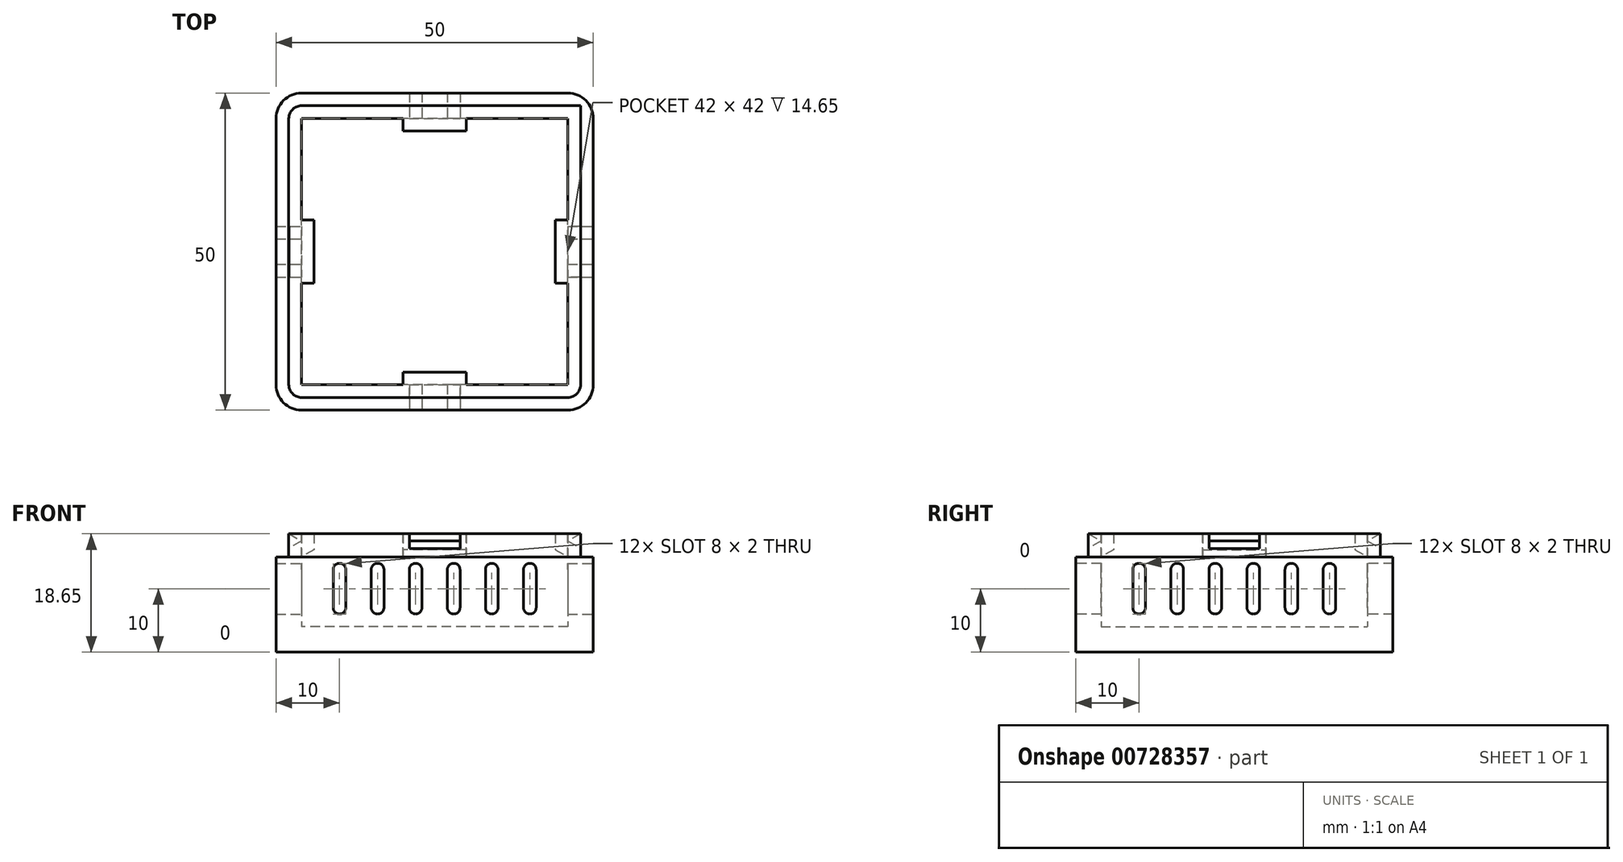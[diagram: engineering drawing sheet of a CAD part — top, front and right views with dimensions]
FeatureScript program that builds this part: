
annotation { "Feature Type Name" : "Feature", "Feature Type Description" : "" }
export const myFeature = defineFeature(function(context is Context, id is Id, definition is map)
    precondition{}
    {
        {
            var Q0;
            Q0=qCreatedBy(makeId("Top.planeOp"),FACE);
            var sketch = newSketch(context, id + "F0", { "sketchPlane" : qUnion([Q0])});
            skLineSegment(sketch, "E0.bottom", {"start": v(25, -25) * mm, "end": v(-25, -25) * mm});
            skLineSegment(sketch, "E0.top", {"start": v(25, 25) * mm, "end": v(-25, 25) * mm});
            skLineSegment(sketch, "E0.left", {"start": v(25, -25) * mm, "end": v(25, 25) * mm});
            skLineSegment(sketch, "E0.right", {"start": v(-25, -25) * mm, "end": v(-25, 25) * mm});
            skPoint(sketch, "E0.middle", {"position": v(0, 0) * mm});
            skSolve(sketch);
        }
        {
            var Q0;
            Q0=qSketchRegion(id+"F0",true);
            extrude(context, id + "F1", {"entities" : qUnion([Q0]), "depth" : 20 * mm, "offsetDistance" : 25 * mm});
        }
        {
            var Q0;
            Q0=makeQuery(id+"F1.opExtrude","CAP_FACE",FACE,{"disambiguationData":[OSD([sQuery(id+"F0.wireOp",EDGE,"E0.bottom"),sQuery(id+"F0.wireOp",EDGE,"E0.top"),sQuery(id+"F0.wireOp",EDGE,"E0.left"),sQuery(id+"F0.wireOp",EDGE,"E0.right")])],"isStart":false});
            shell(context, id + "F2", {"entities" : qUnion([Q0]), "thickness" : 4 * mm});
        }
        {
            var Q0;
            Q0=makeQuery(id+"F1.opExtrude","SWEPT_EDGE",EDGE,{"disambiguationData":[OSD([sQuery(id+"F0.wireOp",EDGE,"E0.bottom"),sQuery(id+"F0.wireOp",EDGE,"E0.right")])]});
            var Q1;
            Q1=makeQuery(id+"F1.opExtrude","SWEPT_EDGE",EDGE,{"disambiguationData":[OSD([sQuery(id+"F0.wireOp",EDGE,"E0.bottom"),sQuery(id+"F0.wireOp",EDGE,"E0.left")])]});
            var Q2;
            Q2=makeQuery(id+"F1.opExtrude","SWEPT_EDGE",EDGE,{"disambiguationData":[OSD([sQuery(id+"F0.wireOp",EDGE,"E0.top"),sQuery(id+"F0.wireOp",EDGE,"E0.left")])]});
            var Q3;
            Q3=makeQuery(id+"F1.opExtrude","SWEPT_EDGE",EDGE,{"disambiguationData":[OSD([sQuery(id+"F0.wireOp",EDGE,"E0.top"),sQuery(id+"F0.wireOp",EDGE,"E0.right")])]});
            fillet(context, id + "F3", {"entities" : qUnion([Q0, Q1, Q2, Q3]), "radius" : 4 * mm, "tangentPropagation" : true, "allowEdgeOverflow" : false});
        }
        {
            var Q0;
            Q0=makeQuery(id+"F1.opExtrude","SWEPT_FACE",FACE,{"disambiguationData":[OSD([sQuery(id+"F0.wireOp",EDGE,"E0.bottom")])]});
            var sketch = newSketch(context, id + "F4", { "sketchPlane" : qUnion([Q0])});
            skLineSegment(sketch, "E1.bottom", {"start": v(-15, 6) * mm, "end": v(-15, 6) * mm});
            skLineSegment(sketch, "E1.top", {"start": v(-15, 14) * mm, "end": v(-15, 14) * mm});
            skLineSegment(sketch, "E1.left", {"start": v(-14, 7) * mm, "end": v(-14, 13) * mm});
            skLineSegment(sketch, "E1.right", {"start": v(-16, 7) * mm, "end": v(-16, 13) * mm});
            skPoint(sketch, "E1.middle", {"position": v(-15, 10) * mm});
            skLineSegment(sketch, "E2.1.0.0", {"start": v(-9, 14) * mm, "end": v(-9, 14) * mm});
            skLineSegment(sketch, "E2.1.0.1", {"start": v(-10, 7) * mm, "end": v(-10, 13) * mm});
            skLineSegment(sketch, "E2.1.0.2", {"start": v(-9, 6) * mm, "end": v(-9, 6) * mm});
            skLineSegment(sketch, "E2.1.0.3", {"start": v(-8, 7) * mm, "end": v(-8, 13) * mm});
            skPoint(sketch, "E2.1.0.4", {"position": v(-9, 10) * mm});
            skLineSegment(sketch, "E2.2.0.0", {"start": v(-3, 14) * mm, "end": v(-3, 14) * mm});
            skLineSegment(sketch, "E2.2.0.1", {"start": v(-4, 7) * mm, "end": v(-4, 13) * mm});
            skLineSegment(sketch, "E2.2.0.2", {"start": v(-3, 6) * mm, "end": v(-3, 6) * mm});
            skLineSegment(sketch, "E2.2.0.3", {"start": v(-2, 7) * mm, "end": v(-2, 13) * mm});
            skPoint(sketch, "E2.2.0.4", {"position": v(-3, 10) * mm});
            skLineSegment(sketch, "E2.3.0.0", {"start": v(3, 14) * mm, "end": v(3, 14) * mm});
            skLineSegment(sketch, "E2.3.0.1", {"start": v(2, 7) * mm, "end": v(2, 13) * mm});
            skLineSegment(sketch, "E2.3.0.2", {"start": v(3, 6) * mm, "end": v(3, 6) * mm});
            skLineSegment(sketch, "E2.3.0.3", {"start": v(4, 7) * mm, "end": v(4, 13) * mm});
            skPoint(sketch, "E2.3.0.4", {"position": v(3, 10) * mm});
            skLineSegment(sketch, "E2.4.0.0", {"start": v(9, 14) * mm, "end": v(9, 14) * mm});
            skLineSegment(sketch, "E2.4.0.1", {"start": v(8, 7) * mm, "end": v(8, 13) * mm});
            skLineSegment(sketch, "E2.4.0.2", {"start": v(9, 6) * mm, "end": v(9, 6) * mm});
            skLineSegment(sketch, "E2.4.0.3", {"start": v(10, 7) * mm, "end": v(10, 13) * mm});
            skPoint(sketch, "E2.4.0.4", {"position": v(9, 10) * mm});
            skLineSegment(sketch, "E2.direction1", {"start": v(-16, 6) * mm, "end": v(-10, 6) * mm, "construction": true});
            skLineSegment(sketch, "E3.MirrorCS", {"start": v(15, 6) * mm, "end": v(15, 6) * mm});
            skLineSegment(sketch, "E4.MirrorCS", {"start": v(16, 7) * mm, "end": v(16, 13) * mm});
            skLineSegment(sketch, "E5.MirrorCS", {"start": v(14, 7) * mm, "end": v(14, 13) * mm});
            skLineSegment(sketch, "E6.MirrorCS", {"start": v(15, 14) * mm, "end": v(15, 14) * mm});
            skPoint(sketch, "E7.MirrorP", {"position": v(15, 10) * mm});
            skLineSegment(sketch, "E8.MirrorCS", {"start": v(16, 6) * mm, "end": v(10, 6) * mm, "construction": true});
            skPoint(sketch, "E9.visualSharp", {"position": v(-16, 14) * mm});
            skArc(sketch, "E9.filletArc", {"start": v(-15, 14) * mm, "mid": v(-15.7, 13.7) * mm, "end": v(-16, 13) * mm});
            skPoint(sketch, "E10.visualSharp", {"position": v(-14, 14) * mm});
            skArc(sketch, "E10.filletArc", {"start": v(-14, 13) * mm, "mid": v(-14.3, 13.7) * mm, "end": v(-15, 14) * mm});
            skPoint(sketch, "E11.visualSharp", {"position": v(-16, 6) * mm});
            skArc(sketch, "E11.filletArc", {"start": v(-16, 7) * mm, "mid": v(-15.7, 6.3) * mm, "end": v(-15, 6) * mm});
            skPoint(sketch, "E12.visualSharp", {"position": v(-14, 6) * mm});
            skArc(sketch, "E12.filletArc", {"start": v(-15, 6) * mm, "mid": v(-14.3, 6.3) * mm, "end": v(-14, 7) * mm});
            skPoint(sketch, "E13.visualSharp", {"position": v(-10, 14) * mm});
            skArc(sketch, "E13.filletArc", {"start": v(-9, 14) * mm, "mid": v(-9.7, 13.7) * mm, "end": v(-10, 13) * mm});
            skPoint(sketch, "E14.visualSharp", {"position": v(-8, 14) * mm});
            skArc(sketch, "E14.filletArc", {"start": v(-8, 13) * mm, "mid": v(-8.3, 13.7) * mm, "end": v(-9, 14) * mm});
            skPoint(sketch, "E15.visualSharp", {"position": v(-8, 6) * mm});
            skArc(sketch, "E15.filletArc", {"start": v(-9, 6) * mm, "mid": v(-8.3, 6.3) * mm, "end": v(-8, 7) * mm});
            skPoint(sketch, "E16.visualSharp", {"position": v(-10, 6) * mm});
            skArc(sketch, "E16.filletArc", {"start": v(-10, 7) * mm, "mid": v(-9.7, 6.3) * mm, "end": v(-9, 6) * mm});
            skPoint(sketch, "E17.visualSharp", {"position": v(-4, 6) * mm});
            skArc(sketch, "E17.filletArc", {"start": v(-4, 7) * mm, "mid": v(-3.7, 6.3) * mm, "end": v(-3, 6) * mm});
            skPoint(sketch, "E18.visualSharp", {"position": v(-2, 6) * mm});
            skArc(sketch, "E18.filletArc", {"start": v(-3, 6) * mm, "mid": v(-2.3, 6.3) * mm, "end": v(-2, 7) * mm});
            skPoint(sketch, "E19.visualSharp", {"position": v(-2, 14) * mm});
            skArc(sketch, "E19.filletArc", {"start": v(-2, 13) * mm, "mid": v(-2.3, 13.7) * mm, "end": v(-3, 14) * mm});
            skPoint(sketch, "E20.visualSharp", {"position": v(-4, 14) * mm});
            skArc(sketch, "E20.filletArc", {"start": v(-3, 14) * mm, "mid": v(-3.7, 13.7) * mm, "end": v(-4, 13) * mm});
            skPoint(sketch, "E21.visualSharp", {"position": v(2, 14) * mm});
            skArc(sketch, "E21.filletArc", {"start": v(3, 14) * mm, "mid": v(2.3, 13.7) * mm, "end": v(2, 13) * mm});
            skPoint(sketch, "E22.visualSharp", {"position": v(4, 14) * mm});
            skArc(sketch, "E22.filletArc", {"start": v(4, 13) * mm, "mid": v(3.7, 13.7) * mm, "end": v(3, 14) * mm});
            skPoint(sketch, "E23.visualSharp", {"position": v(4, 6) * mm});
            skArc(sketch, "E23.filletArc", {"start": v(3, 6) * mm, "mid": v(3.7, 6.3) * mm, "end": v(4, 7) * mm});
            skPoint(sketch, "E24.visualSharp", {"position": v(2, 6) * mm});
            skArc(sketch, "E24.filletArc", {"start": v(2, 7) * mm, "mid": v(2.3, 6.3) * mm, "end": v(3, 6) * mm});
            skPoint(sketch, "E25.visualSharp", {"position": v(10, 14) * mm});
            skArc(sketch, "E25.filletArc", {"start": v(10, 13) * mm, "mid": v(9.7, 13.7) * mm, "end": v(9, 14) * mm});
            skPoint(sketch, "E26.visualSharp", {"position": v(8, 14) * mm});
            skArc(sketch, "E26.filletArc", {"start": v(9, 14) * mm, "mid": v(8.3, 13.7) * mm, "end": v(8, 13) * mm});
            skPoint(sketch, "E27.visualSharp", {"position": v(8, 6) * mm});
            skArc(sketch, "E27.filletArc", {"start": v(8, 7) * mm, "mid": v(8.3, 6.3) * mm, "end": v(9, 6) * mm});
            skPoint(sketch, "E28.visualSharp", {"position": v(10, 6) * mm});
            skArc(sketch, "E28.filletArc", {"start": v(9, 6) * mm, "mid": v(9.7, 6.3) * mm, "end": v(10, 7) * mm});
            skPoint(sketch, "E29.visualSharp", {"position": v(16, 14) * mm});
            skArc(sketch, "E29.filletArc", {"start": v(16, 13) * mm, "mid": v(15.7, 13.7) * mm, "end": v(15, 14) * mm});
            skPoint(sketch, "E30.visualSharp", {"position": v(14, 14) * mm});
            skArc(sketch, "E30.filletArc", {"start": v(15, 14) * mm, "mid": v(14.3, 13.7) * mm, "end": v(14, 13) * mm});
            skPoint(sketch, "E31.visualSharp", {"position": v(16, 6) * mm});
            skArc(sketch, "E31.filletArc", {"start": v(15, 6) * mm, "mid": v(15.7, 6.3) * mm, "end": v(16, 7) * mm});
            skPoint(sketch, "E32.visualSharp", {"position": v(14, 6) * mm});
            skArc(sketch, "E32.filletArc", {"start": v(14, 7) * mm, "mid": v(14.3, 6.3) * mm, "end": v(15, 6) * mm});
            skSolve(sketch);
        }
        {
            var Q0;
            Q0=qSketchRegion(id+"F4",true);
            extrude(context, id + "F5", {"entities" : qUnion([Q0]), "operationType" : NewBodyOperationType.REMOVE, "oppositeDirection" : true, "depth" : 50 * mm, "offsetDistance" : 25 * mm});
        }
        {
            var Q0;
            Q0=makeQuery(id+"F1.opExtrude","SWEPT_FACE",FACE,{"disambiguationData":[OSD([sQuery(id+"F0.wireOp",EDGE,"E0.left")])]});
            var sketch = newSketch(context, id + "F6", { "sketchPlane" : qUnion([Q0])});
            skLineSegment(sketch, "E33.bottom", {"start": v(-15, 6) * mm, "end": v(-15, 6) * mm});
            skLineSegment(sketch, "E33.top", {"start": v(-15, 14) * mm, "end": v(-15, 14) * mm});
            skLineSegment(sketch, "E33.left", {"start": v(-14, 7) * mm, "end": v(-14, 13) * mm});
            skLineSegment(sketch, "E33.right", {"start": v(-16, 7) * mm, "end": v(-16, 13) * mm});
            skPoint(sketch, "E33.middle", {"position": v(-15, 10) * mm});
            skPoint(sketch, "E34.visualSharp", {"position": v(-16, 14) * mm});
            skArc(sketch, "E34.filletArc", {"start": v(-15, 14) * mm, "mid": v(-15.7, 13.7) * mm, "end": v(-16, 13) * mm});
            skPoint(sketch, "E35.visualSharp", {"position": v(-14, 14) * mm});
            skArc(sketch, "E35.filletArc", {"start": v(-14, 13) * mm, "mid": v(-14.3, 13.7) * mm, "end": v(-15, 14) * mm});
            skPoint(sketch, "E36.visualSharp", {"position": v(-14, 6) * mm});
            skArc(sketch, "E36.filletArc", {"start": v(-15, 6) * mm, "mid": v(-14.3, 6.3) * mm, "end": v(-14, 7) * mm});
            skPoint(sketch, "E37.visualSharp", {"position": v(-16, 6) * mm});
            skArc(sketch, "E37.filletArc", {"start": v(-16, 7) * mm, "mid": v(-15.7, 6.3) * mm, "end": v(-15, 6) * mm});
            skPoint(sketch, "E38.1.0.0", {"position": v(-8, 6) * mm});
            skPoint(sketch, "E38.1.0.1", {"position": v(-10, 6) * mm});
            skLineSegment(sketch, "E38.1.0.2", {"start": v(-10, 7) * mm, "end": v(-10, 13) * mm});
            skLineSegment(sketch, "E38.1.0.3", {"start": v(-8, 7) * mm, "end": v(-8, 13) * mm});
            skPoint(sketch, "E38.1.0.4", {"position": v(-8, 14) * mm});
            skPoint(sketch, "E38.1.0.5", {"position": v(-10, 14) * mm});
            skPoint(sketch, "E38.1.0.6", {"position": v(-9, 10) * mm});
            skArc(sketch, "E38.1.0.7", {"start": v(-9, 6) * mm, "mid": v(-8.3, 6.3) * mm, "end": v(-8, 7) * mm});
            skArc(sketch, "E38.1.0.8", {"start": v(-8, 13) * mm, "mid": v(-8.3, 13.7) * mm, "end": v(-9, 14) * mm});
            skArc(sketch, "E38.1.0.9", {"start": v(-9, 14) * mm, "mid": v(-9.7, 13.7) * mm, "end": v(-10, 13) * mm});
            skArc(sketch, "E38.1.0.10", {"start": v(-10, 7) * mm, "mid": v(-9.7, 6.3) * mm, "end": v(-9, 6) * mm});
            skPoint(sketch, "E38.2.0.0", {"position": v(-2, 6) * mm});
            skPoint(sketch, "E38.2.0.1", {"position": v(-4, 6) * mm});
            skLineSegment(sketch, "E38.2.0.2", {"start": v(-4, 7) * mm, "end": v(-4, 13) * mm});
            skLineSegment(sketch, "E38.2.0.3", {"start": v(-2, 7) * mm, "end": v(-2, 13) * mm});
            skPoint(sketch, "E38.2.0.4", {"position": v(-2, 14) * mm});
            skPoint(sketch, "E38.2.0.5", {"position": v(-4, 14) * mm});
            skPoint(sketch, "E38.2.0.6", {"position": v(-3, 10) * mm});
            skArc(sketch, "E38.2.0.7", {"start": v(-3, 6) * mm, "mid": v(-2.3, 6.3) * mm, "end": v(-2, 7) * mm});
            skArc(sketch, "E38.2.0.8", {"start": v(-2, 13) * mm, "mid": v(-2.3, 13.7) * mm, "end": v(-3, 14) * mm});
            skArc(sketch, "E38.2.0.9", {"start": v(-3, 14) * mm, "mid": v(-3.7, 13.7) * mm, "end": v(-4, 13) * mm});
            skArc(sketch, "E38.2.0.10", {"start": v(-4, 7) * mm, "mid": v(-3.7, 6.3) * mm, "end": v(-3, 6) * mm});
            skLineSegment(sketch, "E38.direction1", {"start": v(-16, 6) * mm, "end": v(-10, 6) * mm, "construction": true});
            skArc(sketch, "E39.MirrorCS", {"start": v(10, 7) * mm, "mid": v(9.7, 6.3) * mm, "end": v(9, 6) * mm});
            skArc(sketch, "E40.MirrorCS", {"start": v(9, 14) * mm, "mid": v(9.7, 13.7) * mm, "end": v(10, 13) * mm});
            skArc(sketch, "E41.MirrorCS", {"start": v(9, 6) * mm, "mid": v(8.3, 6.3) * mm, "end": v(8, 7) * mm});
            skArc(sketch, "E42.MirrorCS", {"start": v(16, 7) * mm, "mid": v(15.7, 6.3) * mm, "end": v(15, 6) * mm});
            skArc(sketch, "E43.MirrorCS", {"start": v(15, 6) * mm, "mid": v(14.3, 6.3) * mm, "end": v(14, 7) * mm});
            skArc(sketch, "E44.MirrorCS", {"start": v(14, 13) * mm, "mid": v(14.3, 13.7) * mm, "end": v(15, 14) * mm});
            skArc(sketch, "E45.MirrorCS", {"start": v(2, 13) * mm, "mid": v(2.3, 13.7) * mm, "end": v(3, 14) * mm});
            skArc(sketch, "E46.MirrorCS", {"start": v(3, 6) * mm, "mid": v(2.3, 6.3) * mm, "end": v(2, 7) * mm});
            skArc(sketch, "E47.MirrorCS", {"start": v(4, 7) * mm, "mid": v(3.7, 6.3) * mm, "end": v(3, 6) * mm});
            skArc(sketch, "E48.MirrorCS", {"start": v(8, 13) * mm, "mid": v(8.3, 13.7) * mm, "end": v(9, 14) * mm});
            skArc(sketch, "E49.MirrorCS", {"start": v(15, 14) * mm, "mid": v(15.7, 13.7) * mm, "end": v(16, 13) * mm});
            skArc(sketch, "E50.MirrorCS", {"start": v(3, 14) * mm, "mid": v(3.7, 13.7) * mm, "end": v(4, 13) * mm});
            skPoint(sketch, "E51.MirrorP", {"position": v(9, 10) * mm});
            skLineSegment(sketch, "E52.MirrorCS", {"start": v(4, 7) * mm, "end": v(4, 13) * mm});
            skLineSegment(sketch, "E53.MirrorCS", {"start": v(16, 6) * mm, "end": v(10, 6) * mm, "construction": true});
            skPoint(sketch, "E54.MirrorP", {"position": v(14, 14) * mm});
            skLineSegment(sketch, "E55.MirrorCS", {"start": v(8, 7) * mm, "end": v(8, 13) * mm});
            skPoint(sketch, "E56.MirrorP", {"position": v(4, 6) * mm});
            skPoint(sketch, "E57.MirrorP", {"position": v(14, 6) * mm});
            skPoint(sketch, "E58.MirrorP", {"position": v(4, 14) * mm});
            skLineSegment(sketch, "E59.MirrorCS", {"start": v(10, 7) * mm, "end": v(10, 13) * mm});
            skPoint(sketch, "E60.MirrorP", {"position": v(10, 6) * mm});
            skLineSegment(sketch, "E61.MirrorCS", {"start": v(15, 14) * mm, "end": v(15, 14) * mm});
            skLineSegment(sketch, "E62.MirrorCS", {"start": v(16, 7) * mm, "end": v(16, 13) * mm});
            skLineSegment(sketch, "E63.MirrorCS", {"start": v(14, 7) * mm, "end": v(14, 13) * mm});
            skLineSegment(sketch, "E64.MirrorCS", {"start": v(2, 7) * mm, "end": v(2, 13) * mm});
            skPoint(sketch, "E65.MirrorP", {"position": v(16, 14) * mm});
            skPoint(sketch, "E66.MirrorP", {"position": v(8, 14) * mm});
            skPoint(sketch, "E67.MirrorP", {"position": v(16, 6) * mm});
            skPoint(sketch, "E68.MirrorP", {"position": v(2, 14) * mm});
            skPoint(sketch, "E69.MirrorP", {"position": v(2, 6) * mm});
            skPoint(sketch, "E70.MirrorP", {"position": v(3, 10) * mm});
            skLineSegment(sketch, "E71.MirrorCS", {"start": v(15, 6) * mm, "end": v(15, 6) * mm});
            skPoint(sketch, "E72.MirrorP", {"position": v(15, 10) * mm});
            skPoint(sketch, "E73.MirrorP", {"position": v(8, 6) * mm});
            skPoint(sketch, "E74.MirrorP", {"position": v(10, 14) * mm});
            skSolve(sketch);
        }
        {
            var Q0;
            Q0=qSketchRegion(id+"F6",true);
            extrude(context, id + "F7", {"entities" : qUnion([Q0]), "operationType" : NewBodyOperationType.REMOVE, "endBound" : BoundingType.THROUGH_ALL, "oppositeDirection" : true, "depth" : 25 * mm, "offsetDistance" : 25 * mm});
        }
        {
            var Q0;
            Q0=makeQuery(id+"F1.opExtrude","CAP_FACE",FACE,{"disambiguationData":[OSD([sQuery(id+"F0.wireOp",EDGE,"E0.bottom"),sQuery(id+"F0.wireOp",EDGE,"E0.top"),sQuery(id+"F0.wireOp",EDGE,"E0.left"),sQuery(id+"F0.wireOp",EDGE,"E0.right")])],"isStart":false});
            var sketch = newSketch(context, id + "F8", { "sketchPlane" : qUnion([Q0])});
            skLineSegment(sketch, "E75.bottom", {"start": v(25, 25) * mm, "end": v(-25, 25) * mm});
            skLineSegment(sketch, "E75.top", {"start": v(25, -25) * mm, "end": v(-25, -25) * mm});
            skLineSegment(sketch, "E75.left", {"start": v(25, 25) * mm, "end": v(25, -25) * mm});
            skLineSegment(sketch, "E75.right", {"start": v(-25, 25) * mm, "end": v(-25, -25) * mm});
            skPoint(sketch, "E75.middle", {"position": v(0, 0) * mm});
            skLineSegment(sketch, "E76.bottom", {"start": v(23, 23) * mm, "end": v(-23, 23) * mm});
            skLineSegment(sketch, "E76.top", {"start": v(23, -23) * mm, "end": v(-23, -23) * mm});
            skLineSegment(sketch, "E76.left", {"start": v(23, 23) * mm, "end": v(23, -23) * mm});
            skLineSegment(sketch, "E76.right", {"start": v(-23, 23) * mm, "end": v(-23, -23) * mm});
            skSolve(sketch);
        }
        {
            var Q0;
            Q0=qSketchRegion(id+"F8",true);
            extrude(context, id + "F9", {"entities" : qUnion([Q0]), "operationType" : NewBodyOperationType.REMOVE, "oppositeDirection" : true, "depth" : 5 * mm, "offsetDistance" : 25 * mm});
        }
        {
            var Q0;
            Q0=makeQuery(id+"F9.boolean.opBoolean","COPY",EDGE,{"derivedFrom":makeQuery(id+"F9.opExtrude","SWEPT_EDGE",EDGE,{"disambiguationData":[OSD([sQuery(id+"F8.wireOp",EDGE,"E76.bottom"),sQuery(id+"F8.wireOp",EDGE,"E76.right")])]})});
            var Q1;
            Q1=makeQuery(id+"F9.boolean.opBoolean","COPY",EDGE,{"derivedFrom":makeQuery(id+"F9.opExtrude","SWEPT_EDGE",EDGE,{"disambiguationData":[OSD([sQuery(id+"F8.wireOp",EDGE,"E76.top"),sQuery(id+"F8.wireOp",EDGE,"E76.right")])]})});
            var Q2;
            Q2=makeQuery(id+"F9.boolean.opBoolean","COPY",EDGE,{"derivedFrom":makeQuery(id+"F9.opExtrude","SWEPT_EDGE",EDGE,{"disambiguationData":[OSD([sQuery(id+"F8.wireOp",EDGE,"E76.top"),sQuery(id+"F8.wireOp",EDGE,"E76.left")])]})});
            fillet(context, id + "F10", {"entities" : qUnion([Q0, Q1, Q2]), "radius" : 2 * mm, "tangentPropagation" : true, "allowEdgeOverflow" : false});
        }
        {
            var Q0;
            Q0=qCreatedBy(makeId("Right.planeOp"),FACE);
            var sketch = newSketch(context, id + "F11", { "sketchPlane" : qUnion([Q0])});
            skLineSegment(sketch, "E77", {"start": v(21, 20) * mm, "end": v(19, 18.85) * mm});
            skLineSegment(sketch, "E78", {"start": v(19, 18.85) * mm, "end": v(19, 16.15) * mm});
            skLineSegment(sketch, "E79", {"start": v(19, 16.15) * mm, "end": v(21, 15) * mm});
            skLineSegment(sketch, "E80", {"start": v(21, 15) * mm, "end": v(21, 20) * mm});
            skLineSegment(sketch, "E81.MirrorCS", {"start": v(-21, 20) * mm, "end": v(-19, 18.85) * mm});
            skLineSegment(sketch, "E82.MirrorCS", {"start": v(-19, 18.85) * mm, "end": v(-19, 16.15) * mm});
            skLineSegment(sketch, "E83.MirrorCS", {"start": v(-21, 15) * mm, "end": v(-21, 20) * mm});
            skLineSegment(sketch, "E84.MirrorCS", {"start": v(-19, 16.15) * mm, "end": v(-21, 15) * mm});
            skSolve(sketch);
        }
        {
            var Q0;
            Q0=qSketchRegion(id+"F11",true);
            extrude(context, id + "F12", {"entities" : qUnion([Q0]), "operationType" : NewBodyOperationType.ADD, "endBound" : BoundingType.SYMMETRIC, "depth" : 10 * mm, "offsetDistance" : 25 * mm});
        }
        {
            var Q0;
            Q0=qCreatedBy(makeId("Right.planeOp"),FACE);
            var sketch = newSketch(context, id + "F13", { "sketchPlane" : qUnion([Q0])});
            skLineSegment(sketch, "E85", {"start": v(23, 18.65) * mm, "end": v(21, 17.5) * mm});
            skLineSegment(sketch, "E86", {"start": v(21, 17.5) * mm, "end": v(23, 16.35) * mm});
            skLineSegment(sketch, "E87", {"start": v(23, 16.35) * mm, "end": v(23, 18.65) * mm});
            skLineSegment(sketch, "E88.MirrorCS", {"start": v(-23, 18.65) * mm, "end": v(-21, 17.5) * mm});
            skLineSegment(sketch, "E89.MirrorCS", {"start": v(-21, 17.5) * mm, "end": v(-23, 16.35) * mm});
            skLineSegment(sketch, "E90.MirrorCS", {"start": v(-23, 16.35) * mm, "end": v(-23, 18.65) * mm});
            skSolve(sketch);
        }
        {
            var Q0;
            Q0=qSketchRegion(id+"F13",true);
            extrude(context, id + "F14", {"entities" : qUnion([Q0]), "operationType" : NewBodyOperationType.REMOVE, "endBound" : BoundingType.SYMMETRIC, "oppositeDirection" : true, "depth" : 8 * mm, "offsetDistance" : 25 * mm});
        }
        {
            var Q0;
            Q0=qCreatedBy(makeId("Front.planeOp"),FACE);
            var sketch = newSketch(context, id + "F15", { "sketchPlane" : qUnion([Q0])});
            skLineSegment(sketch, "E91", {"start": v(21, 20) * mm, "end": v(19, 18.85) * mm});
            skLineSegment(sketch, "E92", {"start": v(19, 18.85) * mm, "end": v(19, 16.15) * mm});
            skLineSegment(sketch, "E93", {"start": v(19, 16.15) * mm, "end": v(21, 15) * mm});
            skLineSegment(sketch, "E94", {"start": v(21, 15) * mm, "end": v(21, 20) * mm});
            skLineSegment(sketch, "E95.MirrorCS", {"start": v(-21, 20) * mm, "end": v(-19, 18.85) * mm});
            skLineSegment(sketch, "E96.MirrorCS", {"start": v(-19, 18.85) * mm, "end": v(-19, 16.15) * mm});
            skLineSegment(sketch, "E97.MirrorCS", {"start": v(-21, 15) * mm, "end": v(-21, 20) * mm});
            skLineSegment(sketch, "E98.MirrorCS", {"start": v(-19, 16.15) * mm, "end": v(-21, 15) * mm});
            skSolve(sketch);
        }
        {
            var Q0;
            Q0=qSketchRegion(id+"F15",true);
            extrude(context, id + "F16", {"entities" : qUnion([Q0]), "operationType" : NewBodyOperationType.ADD, "endBound" : BoundingType.SYMMETRIC, "depth" : 10 * mm, "offsetDistance" : 25 * mm});
        }
        {
            var Q0;
            Q0=qCreatedBy(makeId("Front.planeOp"),FACE);
            var sketch = newSketch(context, id + "F17", { "sketchPlane" : qUnion([Q0])});
            skLineSegment(sketch, "E99", {"start": v(23, 18.65) * mm, "end": v(21, 17.5) * mm});
            skLineSegment(sketch, "E100", {"start": v(21, 17.5) * mm, "end": v(23, 16.35) * mm});
            skLineSegment(sketch, "E101", {"start": v(23, 16.35) * mm, "end": v(23, 18.65) * mm});
            skLineSegment(sketch, "E102.MirrorCS", {"start": v(-23, 18.65) * mm, "end": v(-21, 17.5) * mm});
            skLineSegment(sketch, "E103.MirrorCS", {"start": v(-21, 17.5) * mm, "end": v(-23, 16.35) * mm});
            skLineSegment(sketch, "E104.MirrorCS", {"start": v(-23, 16.35) * mm, "end": v(-23, 18.65) * mm});
            skSolve(sketch);
        }
        {
            var Q0;
            Q0=qSketchRegion(id+"F17",true);
            extrude(context, id + "F18", {"entities" : qUnion([Q0]), "operationType" : NewBodyOperationType.REMOVE, "endBound" : BoundingType.SYMMETRIC, "oppositeDirection" : true, "depth" : 8 * mm, "offsetDistance" : 25 * mm});
        }
        {
            var Q0;
            Q0=makeQuery(id+"F1.opExtrude","CAP_FACE",FACE,{"disambiguationData":[OSD([sQuery(id+"F0.wireOp",EDGE,"E0.bottom"),sQuery(id+"F0.wireOp",EDGE,"E0.top"),sQuery(id+"F0.wireOp",EDGE,"E0.left"),sQuery(id+"F0.wireOp",EDGE,"E0.right")])],"isStart":false});
            var sketch = newSketch(context, id + "F19", { "sketchPlane" : qUnion([Q0])});
            skLineSegment(sketch, "E105.bottom", {"start": v(23, -23) * mm, "end": v(-23, -23) * mm});
            skLineSegment(sketch, "E105.top", {"start": v(23, 23) * mm, "end": v(-23, 23) * mm});
            skLineSegment(sketch, "E105.left", {"start": v(23, -23) * mm, "end": v(23, 23) * mm});
            skLineSegment(sketch, "E105.right", {"start": v(-23, -23) * mm, "end": v(-23, 23) * mm});
            skPoint(sketch, "E105.middle", {"position": v(0, 0) * mm});
            skSolve(sketch);
        }
        {
            var Q0;
            Q0=qSketchRegion(id+"F19",true);
            extrude(context, id + "F20", {"entities" : qUnion([Q0]), "operationType" : NewBodyOperationType.REMOVE, "oppositeDirection" : true, "depth" : 1.35 * mm, "offsetDistance" : 25 * mm});
        }
    });
